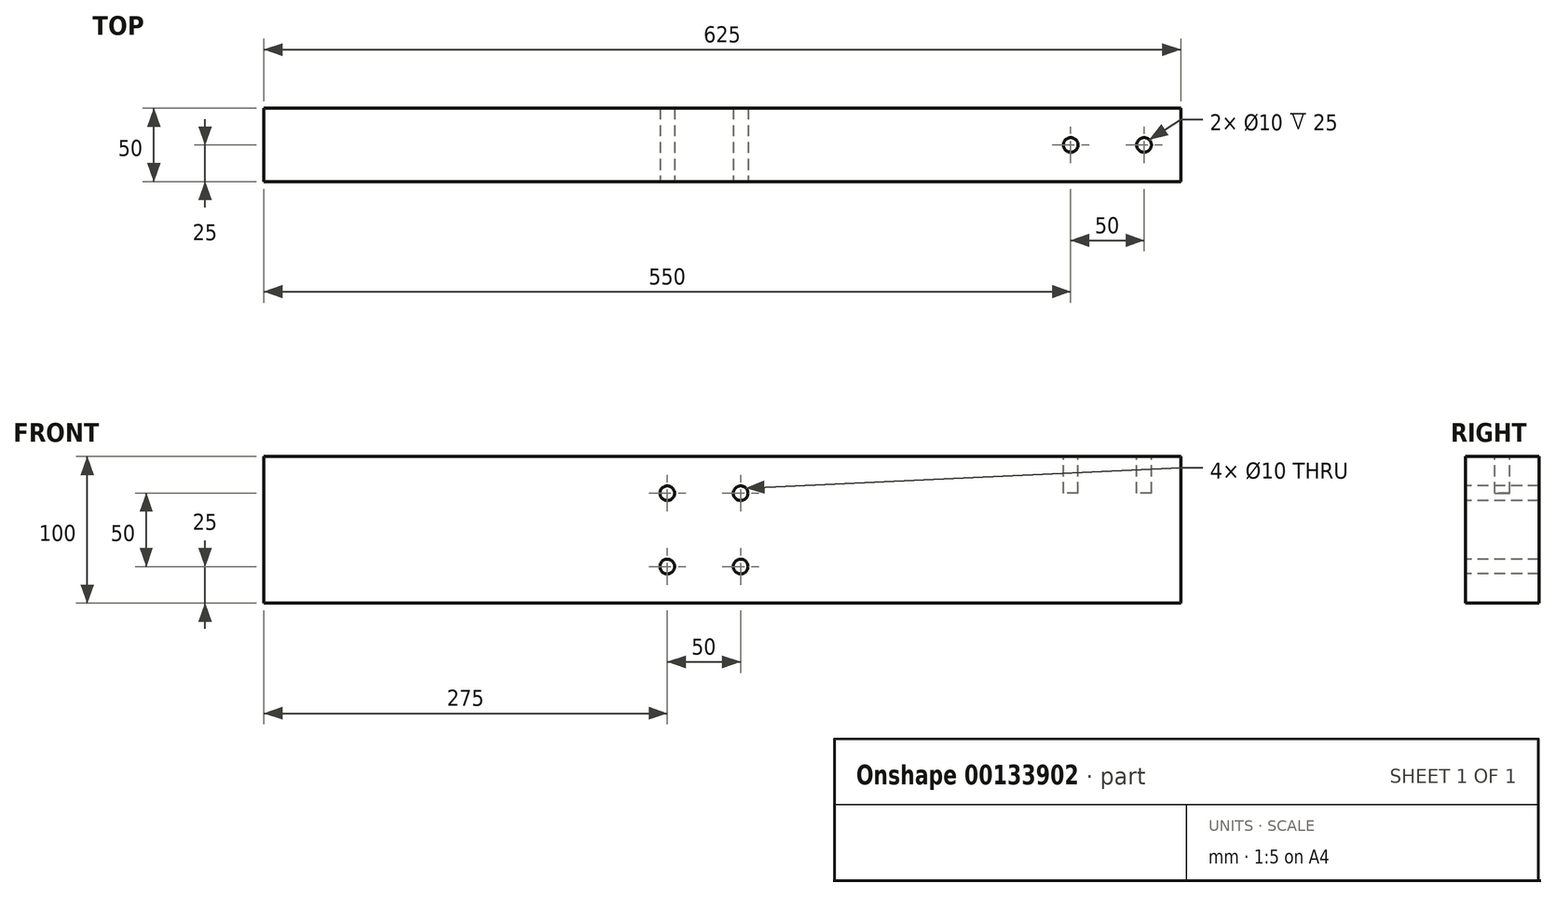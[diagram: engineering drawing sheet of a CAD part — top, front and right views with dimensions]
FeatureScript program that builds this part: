
annotation { "Feature Type Name" : "Feature", "Feature Type Description" : "" }
export const myFeature = defineFeature(function(context is Context, id is Id, definition is map)
    precondition{}
    {
        {
            var Q0;
            Q0=qCreatedBy(makeId("Front.planeOp"),FACE);
            var sketch = newSketch(context, id + "F0", { "sketchPlane" : qUnion([Q0])});
            skLineSegment(sketch, "E0.bottom", {"start": v(312.5, -50) * mm, "end": v(-312.5, -50) * mm});
            skLineSegment(sketch, "E0.top", {"start": v(312.5, 50) * mm, "end": v(-312.5, 50) * mm});
            skLineSegment(sketch, "E0.left", {"start": v(312.5, -50) * mm, "end": v(312.5, 50) * mm});
            skLineSegment(sketch, "E0.right", {"start": v(-312.5, -50) * mm, "end": v(-312.5, 50) * mm});
            skPoint(sketch, "E0.middle", {"position": v(0, 0) * mm});
            skSolve(sketch);
        }
        {
            var Q0;
            Q0=qSketchRegion(id+"F0",true);
            extrude(context, id + "F1", {"entities" : qUnion([Q0]), "depth" : 50 * mm});
        }
        {
            var Q0;
            Q0=makeQuery(id+"F1.opExtrude","CAP_FACE",FACE,{"disambiguationData":[OSD([sQuery(id+"F0.wireOp",EDGE,"E0.bottom"),sQuery(id+"F0.wireOp",EDGE,"E0.top"),sQuery(id+"F0.wireOp",EDGE,"E0.left"),sQuery(id+"F0.wireOp",EDGE,"E0.right")])],"isStart":false});
            var sketch = newSketch(context, id + "F2", { "sketchPlane" : qUnion([Q0])});
            skCircle(sketch, "E1", {"center": v(-37.5, -25) * mm, "radius": 5 * mm});
            skCircle(sketch, "E2", {"center": v(12.5, -25) * mm, "radius": 5 * mm});
            skCircle(sketch, "E3", {"center": v(-37.5, 25) * mm, "radius": 5 * mm});
            skCircle(sketch, "E4", {"center": v(12.5, 25) * mm, "radius": 5 * mm});
            skSolve(sketch);
        }
        {
            var Q0;
            Q0=makeQuery(id+"F2.imprint","IMPRINT",FACE,{"disambiguationData":[TD([[makeQuery(id+"F2.imprint","IMPRINT",EDGE,{"derivedFrom":sQuery(id+"F2.wireOp",EDGE,"E1")}),1.0]])]});
            var Q1;
            Q1=makeQuery(id+"F2.imprint","IMPRINT",FACE,{"disambiguationData":[TD([[makeQuery(id+"F2.imprint","IMPRINT",EDGE,{"derivedFrom":sQuery(id+"F2.wireOp",EDGE,"E2")}),1.0]])]});
            var Q2;
            Q2=makeQuery(id+"F2.imprint","IMPRINT",FACE,{"disambiguationData":[TD([[makeQuery(id+"F2.imprint","IMPRINT",EDGE,{"derivedFrom":sQuery(id+"F2.wireOp",EDGE,"E3")}),1.0]])]});
            var Q3;
            Q3=makeQuery(id+"F2.imprint","IMPRINT",FACE,{"disambiguationData":[TD([[makeQuery(id+"F2.imprint","IMPRINT",EDGE,{"derivedFrom":sQuery(id+"F2.wireOp",EDGE,"E4")}),1.0]])]});
            extrude(context, id + "F3", {"entities" : qUnion([Q0, Q1, Q2, Q3]), "operationType" : NewBodyOperationType.REMOVE, "oppositeDirection" : true, "depth" : 50 * mm});
        }
        {
            var Q0;
            Q0=makeQuery(id+"F1.opExtrude","SWEPT_FACE",FACE,{"disambiguationData":[OSD([sQuery(id+"F0.wireOp",EDGE,"E0.top")])]});
            var sketch = newSketch(context, id + "F4", { "sketchPlane" : qUnion([Q0])});
            skCircle(sketch, "E5", {"center": v(287.5, -25) * mm, "radius": 5 * mm});
            skPoint(sketch, "E5.centerSnap0", {"position": v(312.5, -25) * mm});
            skCircle(sketch, "E6", {"center": v(237.5, -25) * mm, "radius": 5 * mm});
            skSolve(sketch);
        }
        {
            var Q0;
            Q0=makeQuery(id+"F4.imprint","IMPRINT",FACE,{"disambiguationData":[TD([[makeQuery(id+"F4.imprint","IMPRINT",EDGE,{"derivedFrom":sQuery(id+"F4.wireOp",EDGE,"E6")}),1.0]])]});
            var Q1;
            Q1=makeQuery(id+"F4.imprint","IMPRINT",FACE,{"disambiguationData":[TD([[makeQuery(id+"F4.imprint","IMPRINT",EDGE,{"derivedFrom":sQuery(id+"F4.wireOp",EDGE,"E5")}),1.0]])]});
            extrude(context, id + "F5", {"entities" : qUnion([Q0, Q1]), "operationType" : NewBodyOperationType.REMOVE, "oppositeDirection" : true, "depth" : 25 * mm});
        }
    });
